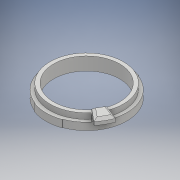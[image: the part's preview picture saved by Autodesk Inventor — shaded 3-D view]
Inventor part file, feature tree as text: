
AUTODESK INVENTOR PART (.ipt)
format: ipt  version: 2018 (Build 220112000, 112)  size: 342,528 bytes
history: native  units: mm
features: extrude x4, sketch x4, chamfer x2, other x1, mirror x1
ambient origin geometry x8: Origin, YZ Plane, XZ Plane, XY Plane, X Axis, Y Axis, Z Axis, Center Point
bodies: Body1 (feature_tree)
feature tree (12):
  other  "ソリッド1"
  extrude  "押し出し1"  Depth=4.65mm
  extrude  "押し出し2"  Depth=40.5mm
  mirror  "ミラー1"
  extrude  "押し出し7"  Depth=8.0mm TaperAngle=0.0deg
  chamfer  "面取り4"  Distance=0.3mm
  extrude  "押し出し8"  Depth=24.43461mm
  chamfer  "面取り5"  Distance=5.0mm
  sketch  "スケッチ1"
  sketch  "スケッチ2"
  sketch  "スケッチ4"
  sketch  "スケッチ7"
